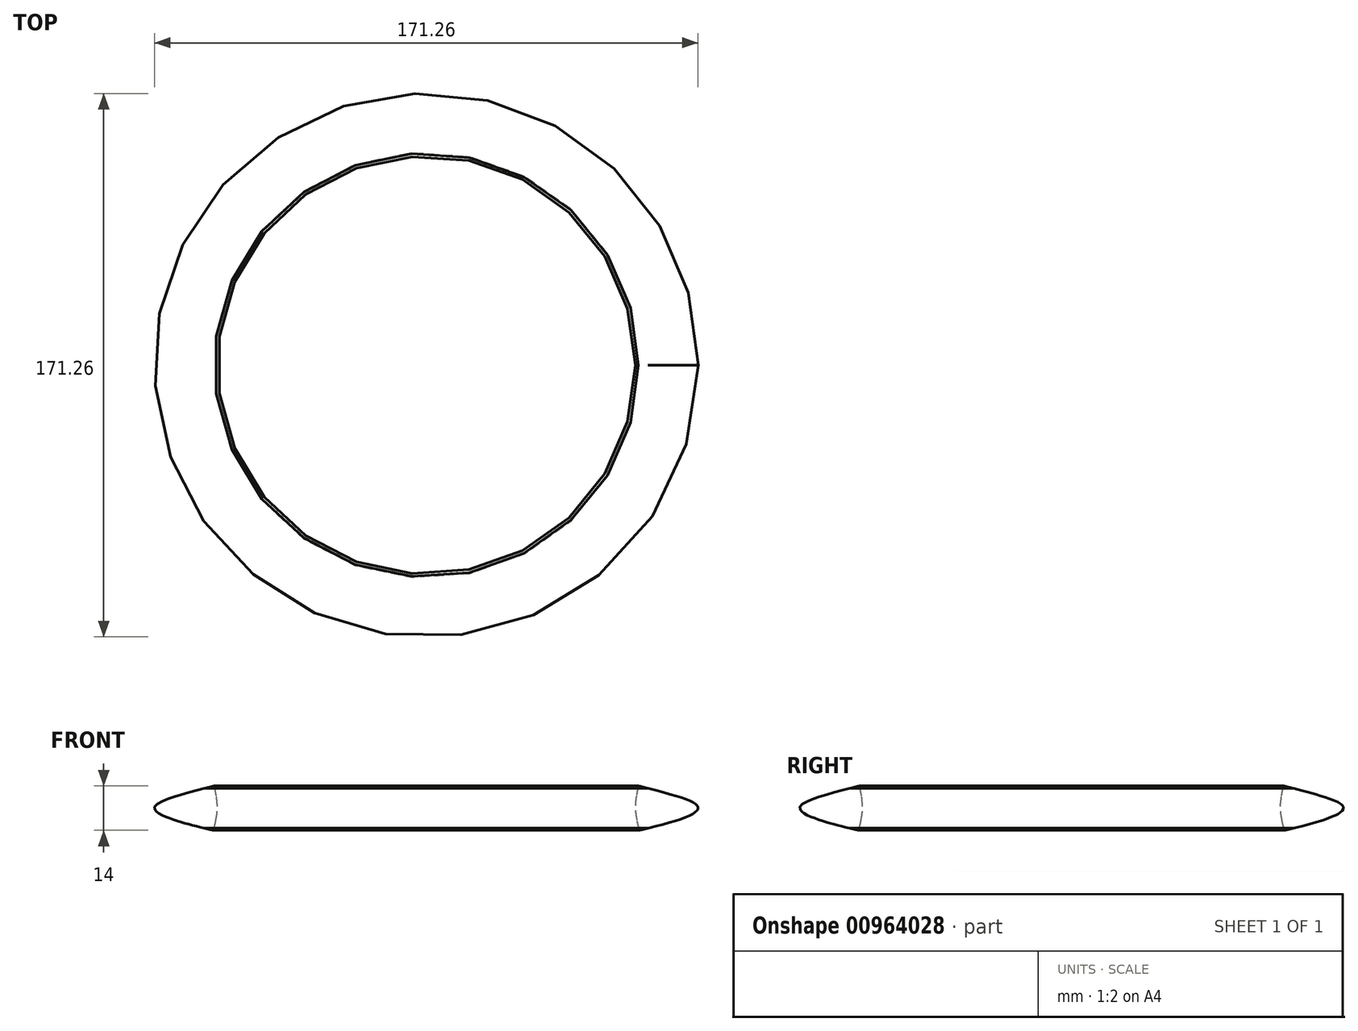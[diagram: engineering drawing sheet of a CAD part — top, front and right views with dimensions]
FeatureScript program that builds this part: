
annotation { "Feature Type Name" : "Feature", "Feature Type Description" : "" }
export const myFeature = defineFeature(function(context is Context, id is Id, definition is map)
    precondition{}
    {
        {
            var Q0;
            Q0=qCreatedBy(makeId("Top.planeOp"),FACE);
            var sketch = newSketch(context, id + "F0", { "sketchPlane" : qUnion([Q0])});
            skCircle(sketch, "E0", {"center": v(0, 0) * mm, "radius": 66.7 * mm});
            skSolve(sketch);
        }
        {
            var Q0;
            Q0=qCreatedBy(makeId("Front.planeOp"),FACE);
            var sketch = newSketch(context, id + "F1", { "sketchPlane" : qUnion([Q0])});
            skLineSegment(sketch, "E1.0", {"start": v(-66.7, 0) * mm, "end": v(66.7, 0) * mm, "construction": true});
            skFitSpline(sketch, "E2", {"points": [v(-66.8, 7) * mm, v(-85.63, 0) * mm, v(-67.03, -7) * mm], "startDerivative": vector(-69.14, -17.56) * mm, "endDerivative": vector(65.68, -14.8) * mm});
            skFitSpline(sketch, "E3", {"points": [v(-66.8, 7) * mm, v(-65.85, 0) * mm, v(-67.03, -7) * mm], "startDerivative": vector(2.95, -14.03) * mm, "endDerivative": vector(-3.41, -13.97) * mm});
            skArc(sketch, "E4.filletArc", {"start": v(-66.17, 3.79) * mm, "mid": v(-67.49, 5.82) * mm, "end": v(-69.87, 6.21) * mm});
            skArc(sketch, "E5.filletArc", {"start": v(-69.97, -6.32) * mm, "mid": v(-67.66, -5.93) * mm, "end": v(-66.34, -4) * mm});
            skLineSegment(sketch, "E6", {"start": v(0, 45.37) * mm, "end": v(0, -52.5) * mm, "construction": true});
            skSolve(sketch);
        }
        {
            var Q0;
            Q0 = qSketchRegion(id + "F1", true);
            var Q1;
            Q1=sQuery(id+"F1.wireOp",EDGE,"E6");
            revolve(context, id + "F2", {"surfaceOperationType" : NewSurfaceOperationType.NEW, "entities" : qUnion([Q0]), "axis" : qUnion([Q1]), "revolveType" : RevolveType.FULL});
        }
    });
